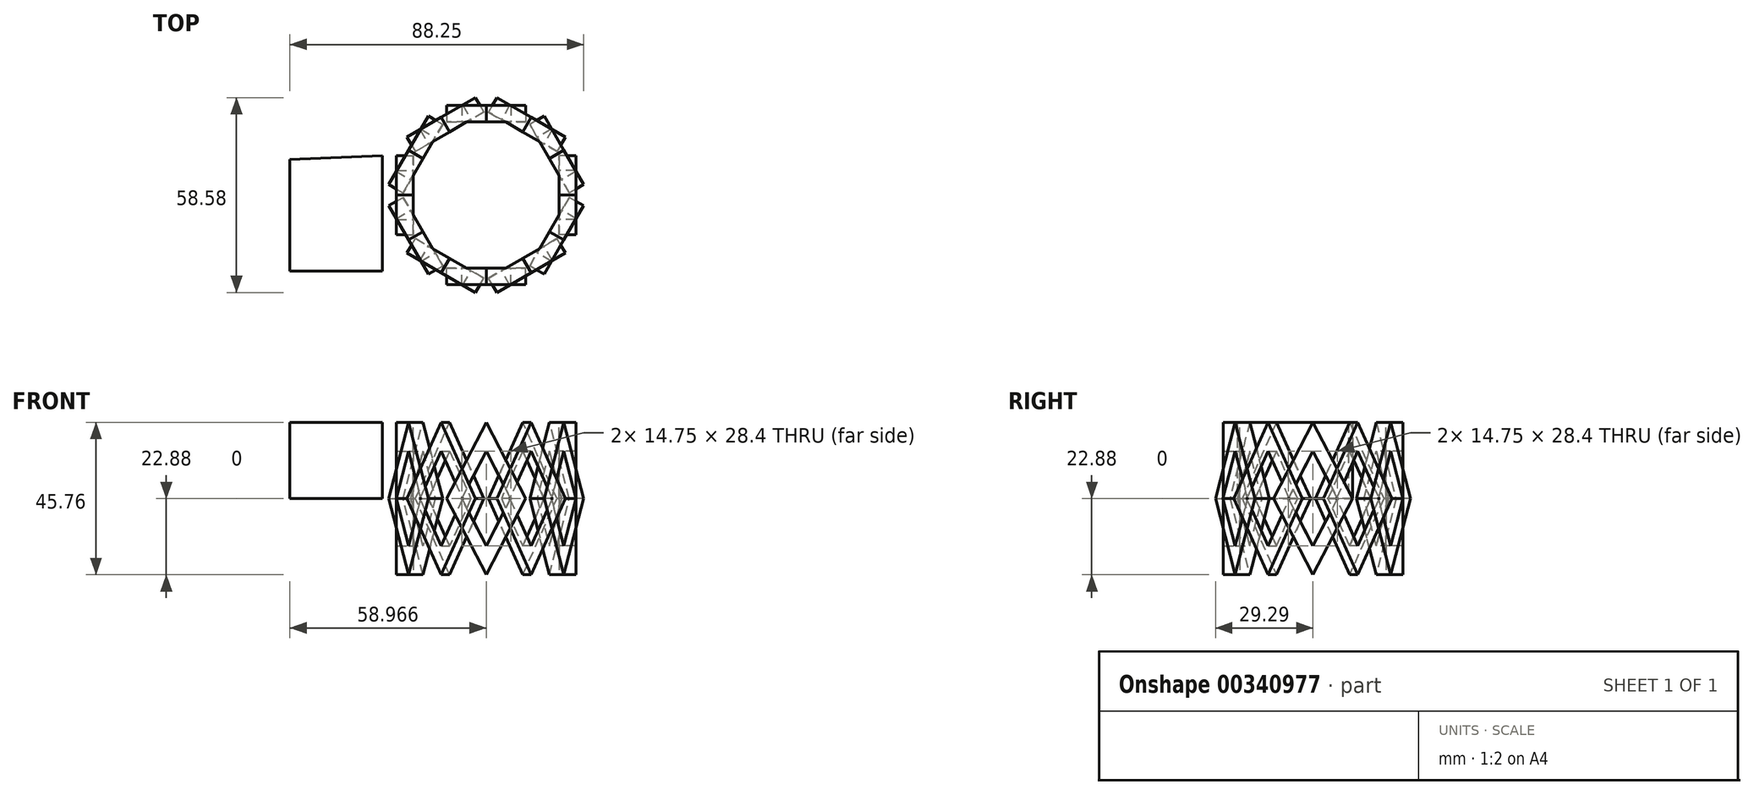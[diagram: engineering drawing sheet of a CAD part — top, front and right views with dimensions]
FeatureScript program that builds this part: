
annotation { "Feature Type Name" : "Feature", "Feature Type Description" : "" }
export const myFeature = defineFeature(function(context is Context, id is Id, definition is map)
    precondition{}
    {
        {
            var Q0;
            Q0=qCreatedBy(makeId("Right.planeOp"),FACE);
            var sketch = newSketch(context, id + "F0", { "sketchPlane" : qUnion([Q0])});
            skLineSegment(sketch, "E0", {"start": v(0, 14.2) * mm, "end": v(-7.37, 0) * mm});
            skLineSegment(sketch, "E1", {"start": v(-7.37, 0) * mm, "end": v(0, -14.2) * mm});
            skLineSegment(sketch, "E2", {"start": v(0, -14.2) * mm, "end": v(7.37, 0) * mm});
            skLineSegment(sketch, "E3", {"start": v(7.37, 0) * mm, "end": v(0, 14.2) * mm});
            skLineSegment(sketch, "E4.0", {"start": v(0, 22.88) * mm, "end": v(-11.88, 0) * mm});
            skLineSegment(sketch, "E4.1", {"start": v(11.88, 0) * mm, "end": v(0, 22.88) * mm});
            skLineSegment(sketch, "E4.2", {"start": v(0, -22.88) * mm, "end": v(11.88, 0) * mm});
            skLineSegment(sketch, "E4.3", {"start": v(-11.88, 0) * mm, "end": v(0, -22.88) * mm});
            skSolve(sketch);
        }
        {
            var Q0;
            Q0=makeQuery(id+"F0.imprint","IMPRINT",FACE,{"disambiguationData":[TD([[makeQuery(id+"F0.imprint","IMPRINT",EDGE,{"derivedFrom":sQuery(id+"F0.wireOp",EDGE,"E0")}),-1.0]])]});
            extrude(context, id + "F1", {"entities" : qUnion([Q0]), "oppositeDirection" : true, "depth" : 5 * mm});
        }
        {
            var Q0;
            Q0=qCreatedBy(makeId("Front.planeOp"),FACE);
            var sketch = newSketch(context, id + "F2", { "sketchPlane" : qUnion([Q0])});
            skLineSegment(sketch, "E5", {"start": v(21.96, 0) * mm, "end": v(21.96, 36.38) * mm});
            skLineSegment(sketch, "E6", {"start": v(21.96, 36.38) * mm, "end": v(21.96, 95.1) * mm});
            skSolve(sketch);
        }
        {
            var Q0;
            Q0=makeQuery(id+"F1.opExtrude","SWEPT_BODY",BODY,{"disambiguationData":[OSD([sQuery(id+"F0.wireOp",EDGE,"E0"),sQuery(id+"F0.wireOp",EDGE,"E1"),sQuery(id+"F0.wireOp",EDGE,"E2"),sQuery(id+"F0.wireOp",EDGE,"E3"),sQuery(id+"F0.wireOp",EDGE,"E4.0"),sQuery(id+"F0.wireOp",EDGE,"E4.1"),sQuery(id+"F0.wireOp",EDGE,"E4.2"),sQuery(id+"F0.wireOp",EDGE,"E4.3")])]});
            var Q1;
            Q1=sQuery(id+"F2.wireOp",EDGE,"E5");
            circularPattern(context, id + "F3", {"entities" : qUnion([Q0]), "axis" : qUnion([Q1]), "angle" : 360 * degree, "instanceCount" : 12, "equalSpace" : true});
        }
        {
            var Q0;
            Q0=qCreatedBy(makeId("Top.planeOp"),FACE);
            var sketch = newSketch(context, id + "F4", { "sketchPlane" : qUnion([Q0])});
            skLineSegment(sketch, "E7", {"start": v(-9.18, 11.84) * mm, "end": v(-9.18, -22.8) * mm});
            skLineSegment(sketch, "E8", {"start": v(-9.18, -22.8) * mm, "end": v(-37, -22.8) * mm});
            skLineSegment(sketch, "E9", {"start": v(-37, -22.8) * mm, "end": v(-37, 10.66) * mm});
            skLineSegment(sketch, "E10", {"start": v(-37, 10.66) * mm, "end": v(-9.18, 11.84) * mm});
            skSolve(sketch);
        }
        {
            var Q0;
            Q0=makeQuery(id+"F4.imprint","IMPRINT",FACE,{"disambiguationData":[TD([[makeQuery(id+"F4.imprint","IMPRINT",EDGE,{"derivedFrom":sQuery(id+"F4.wireOp",EDGE,"E7")}),-1.0]])]});
            extrude(context, id + "F5", {"entities" : qUnion([Q0]), "depth" : 22.88 * mm});
        }
    });
